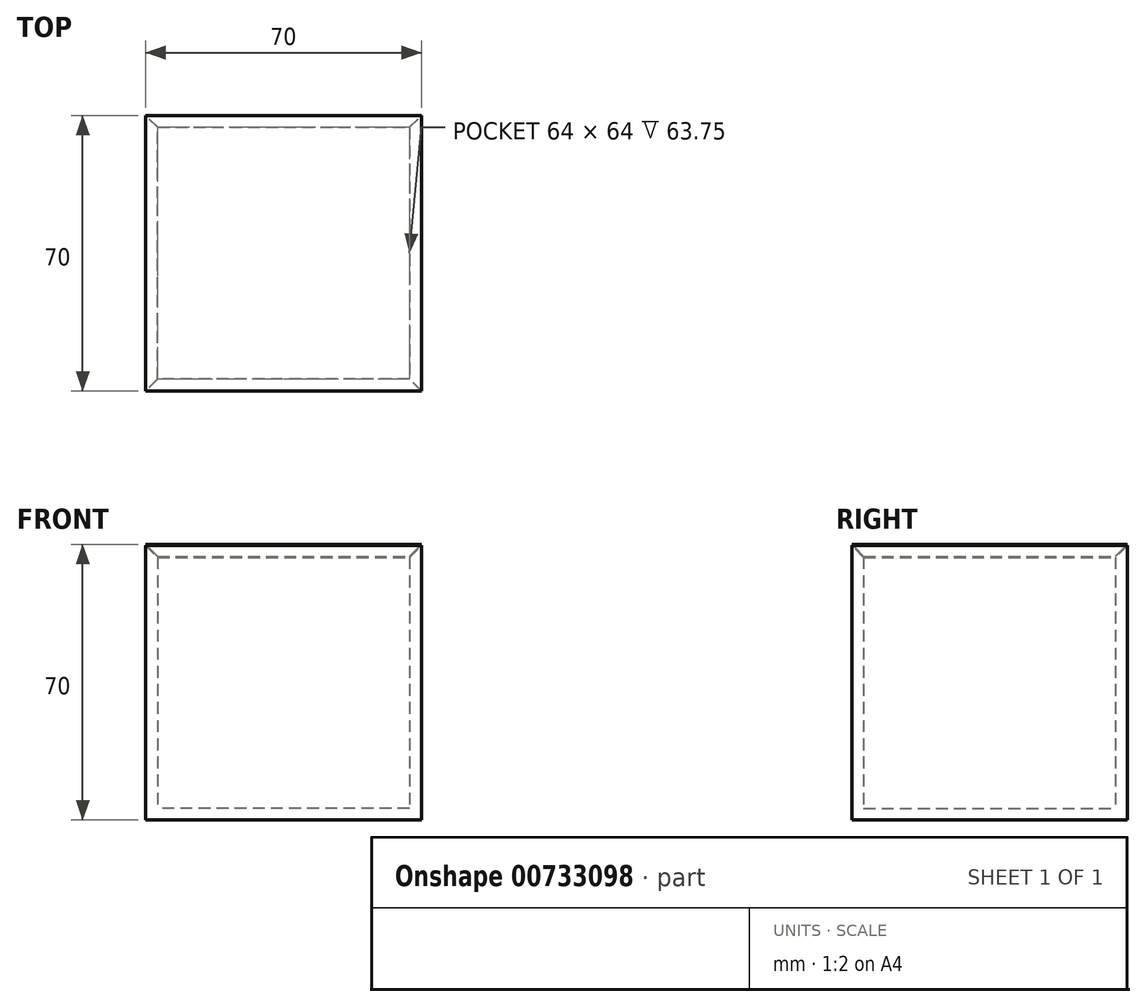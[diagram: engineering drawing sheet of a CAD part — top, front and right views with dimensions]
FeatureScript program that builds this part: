
annotation { "Feature Type Name" : "Feature", "Feature Type Description" : "" }
export const myFeature = defineFeature(function(context is Context, id is Id, definition is map)
    precondition{}
    {
        {
            var Q0;
            Q0=qCreatedBy(makeId("Top.planeOp"),FACE);
            var sketch = newSketch(context, id + "F0", { "sketchPlane" : qUnion([Q0])});
            skLineSegment(sketch, "E0.bottom", {"start": v(35, -35) * mm, "end": v(-35, -35) * mm});
            skLineSegment(sketch, "E0.top", {"start": v(35, 35) * mm, "end": v(-35, 35) * mm});
            skLineSegment(sketch, "E0.left", {"start": v(35, -35) * mm, "end": v(35, 35) * mm});
            skLineSegment(sketch, "E0.right", {"start": v(-35, -35) * mm, "end": v(-35, 35) * mm});
            skPoint(sketch, "E0.middle", {"position": v(0, 0) * mm});
            skSolve(sketch);
        }
        {
            var Q0;
            Q0=makeQuery(id+"F0.imprint","IMPRINT",FACE,{"disambiguationData":[TD([[makeQuery(id+"F0.imprint","IMPRINT",EDGE,{"derivedFrom":sQuery(id+"F0.wireOp",EDGE,"E0.bottom")}),-1.0]])]});
            extrude(context, id + "F1", {"entities" : qUnion([Q0]), "endBound" : BoundingType.SYMMETRIC, "depth" : 70 * mm, "offsetDistance" : 25 * mm});
        }
        {
            var Q0;
            Q0=makeQuery(id+"F1.opExtrude","CAP_FACE",FACE,{"disambiguationData":[OSD([sQuery(id+"F0.wireOp",EDGE,"E0.bottom"),sQuery(id+"F0.wireOp",EDGE,"E0.top"),sQuery(id+"F0.wireOp",EDGE,"E0.left"),sQuery(id+"F0.wireOp",EDGE,"E0.right")])],"isStart":false});
            shell(context, id + "F2", {"entities" : qUnion([Q0]), "thickness" : 3 * mm});
        }
        {
            var Q0;
            Q0=makeQuery(id+"F1.opExtrude","CAP_FACE",FACE,{"disambiguationData":[OSD([sQuery(id+"F0.wireOp",EDGE,"E0.bottom"),sQuery(id+"F0.wireOp",EDGE,"E0.top"),sQuery(id+"F0.wireOp",EDGE,"E0.left"),sQuery(id+"F0.wireOp",EDGE,"E0.right")])],"isStart":false});
            var sketch = newSketch(context, id + "F3", { "sketchPlane" : qUnion([Q0])});
            skLineSegment(sketch, "E1.bottom", {"start": v(-35, 35) * mm, "end": v(35, 35) * mm});
            skLineSegment(sketch, "E1.top", {"start": v(-35, -35) * mm, "end": v(35, -35) * mm});
            skLineSegment(sketch, "E1.left", {"start": v(-35, 35) * mm, "end": v(-35, -35) * mm});
            skLineSegment(sketch, "E1.right", {"start": v(35, 35) * mm, "end": v(35, -35) * mm});
            skSolve(sketch);
        }
        {
            var Q0;
            Q0 = qSketchRegion(id + "F3", true);
            extrude(context, id + "F4", {"entities" : qUnion([Q0]), "oppositeDirection" : true, "depth" : 3 * mm, "offsetDistance" : 25 * mm});
        }
        {
            var Q0;
            Q0=makeQuery(id+"F4.opExtrude","CAP_FACE",FACE,{"disambiguationData":[OSD([sQuery(id+"F3.wireOp",EDGE,"E1.bottom"),sQuery(id+"F3.wireOp",EDGE,"E1.top"),sQuery(id+"F3.wireOp",EDGE,"E1.left"),sQuery(id+"F3.wireOp",EDGE,"E1.right")])],"isStart":false});
            chamfer(context, id + "F5", {"entities" : qUnion([Q0]), "width" : 3 * mm, "tangentPropagation" : true});
        }
        {
            var Q0;
            {var subQ0=sQuery(id+"F0.wireOp",EDGE,"E0.bottom");Q0=makeQuery(id+"F2.opShell","OFFSET_EDGE",EDGE,{"disambiguationData":[OSD([subQ0]),TDD([makeQuery(id+"F1.opExtrude","CAP_EDGE",EDGE,{"disambiguationData":[OSD([subQ0])],"isStart":false})])]});}
            var Q1;
            {var subQ0=sQuery(id+"F0.wireOp",EDGE,"E0.right");Q1=makeQuery(id+"F2.opShell","OFFSET_EDGE",EDGE,{"disambiguationData":[OSD([subQ0]),TDD([makeQuery(id+"F1.opExtrude","CAP_EDGE",EDGE,{"disambiguationData":[OSD([subQ0])],"isStart":false})])]});}
            var Q2;
            {var subQ0=sQuery(id+"F0.wireOp",EDGE,"E0.top");Q2=makeQuery(id+"F2.opShell","OFFSET_EDGE",EDGE,{"disambiguationData":[OSD([subQ0]),TDD([makeQuery(id+"F1.opExtrude","CAP_EDGE",EDGE,{"disambiguationData":[OSD([subQ0])],"isStart":false})])]});}
            var Q3;
            {var subQ0=sQuery(id+"F0.wireOp",EDGE,"E0.left");Q3=makeQuery(id+"F2.opShell","OFFSET_EDGE",EDGE,{"disambiguationData":[OSD([subQ0]),TDD([makeQuery(id+"F1.opExtrude","CAP_EDGE",EDGE,{"disambiguationData":[OSD([subQ0])],"isStart":false})])]});}
            chamfer(context, id + "F6", {"entities" : qUnion([Q0, Q1, Q2, Q3]), "width" : 3.25 * mm, "tangentPropagation" : true});
        }
    });
